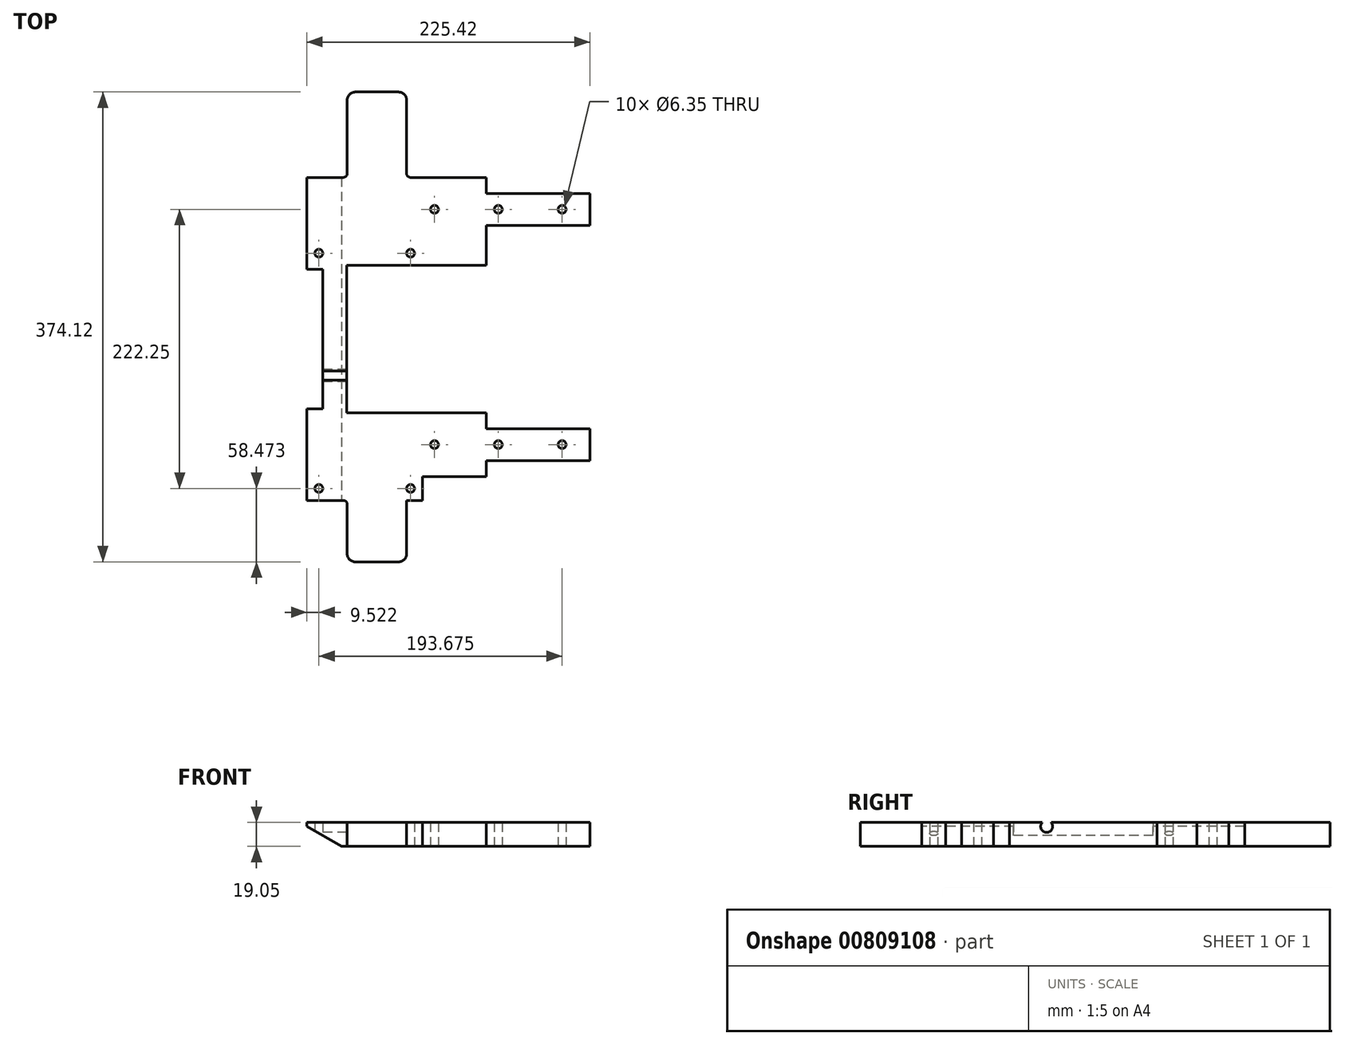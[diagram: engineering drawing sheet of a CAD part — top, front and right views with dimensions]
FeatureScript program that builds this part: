
annotation { "Feature Type Name" : "Feature", "Feature Type Description" : "" }
export const myFeature = defineFeature(function(context is Context, id is Id, definition is map)
    precondition{}
    {
        {
            var Q0;
            Q0=qCreatedBy(makeId("Top.planeOp"),FACE);
            var sketch = newSketch(context, id + "F0", { "sketchPlane" : qUnion([Q0])});
            skLineSegment(sketch, "E0.top", {"start": v(-147.88, 53.82) * mm, "end": v(-118.93, 53.82) * mm});
            skLineSegment(sketch, "E0.right", {"start": v(1.34, 15.72) * mm, "end": v(1.34, 41.12) * mm, "construction": true});
            skLineSegment(sketch, "E1.top", {"start": v(77.54, 41.12) * mm, "end": v(-5, 41.12) * mm});
            skLineSegment(sketch, "E1.right", {"start": v(-5, 53.82) * mm, "end": v(-5, 41.12) * mm});
            skLineSegment(sketch, "E2.top", {"start": v(77.54, 15.72) * mm, "end": v(77.54, 15.72) * mm});
            skLineSegment(sketch, "E2.right", {"start": v(-5, -16.03) * mm, "end": v(-5, 15.72) * mm});
            skLineSegment(sketch, "E3.0", {"start": v(-68.5, 115.47) * mm, "end": v(-68.5, 57) * mm});
            skLineSegment(sketch, "E4.0", {"start": v(-109.4, 121.82) * mm, "end": v(-74.86, 121.82) * mm});
            skLineSegment(sketch, "E5.0", {"start": v(-115.75, 115.47) * mm, "end": v(-115.75, 57) * mm});
            skLineSegment(sketch, "E6.trimOffspring", {"start": v(-65.33, 53.82) * mm, "end": v(-5, 53.82) * mm});
            skPoint(sketch, "E7.visualSharp", {"position": v(-115.75, 121.82) * mm});
            skArc(sketch, "E7.filletArc", {"start": v(-109.4, 121.82) * mm, "mid": v(-113.9, 119.96) * mm, "end": v(-115.75, 115.47) * mm});
            skPoint(sketch, "E8.visualSharp", {"position": v(-68.5, 121.82) * mm});
            skArc(sketch, "E8.filletArc", {"start": v(-68.5, 115.47) * mm, "mid": v(-70.37, 119.96) * mm, "end": v(-74.86, 121.82) * mm});
            skLineSegment(sketch, "E9.0", {"start": v(-109.78, -65.24) * mm, "end": v(-5, -65.24) * mm, "construction": true});
            skArc(sketch, "E10.MirrorCS", {"start": v(-109.4, -252.3) * mm, "mid": v(-113.9, -250.44) * mm, "end": v(-115.75, -245.95) * mm});
            skArc(sketch, "E11.MirrorCS", {"start": v(-68.5, -245.95) * mm, "mid": v(-70.37, -250.44) * mm, "end": v(-74.86, -252.3) * mm});
            skLineSegment(sketch, "E12.MirrorCS", {"start": v(-5, -184.3) * mm, "end": v(-5, -171.6) * mm});
            skLineSegment(sketch, "E13.MirrorCS", {"start": v(77.54, -171.6) * mm, "end": v(-5, -171.6) * mm});
            skLineSegment(sketch, "E14.MirrorCS", {"start": v(77.54, -146.2) * mm, "end": v(-5, -146.2) * mm});
            skLineSegment(sketch, "E15.MirrorCS", {"start": v(-5, -122.48) * mm, "end": v(-5, -146.2) * mm});
            skLineSegment(sketch, "E16.MirrorCS", {"start": v(-147.88, -184.3) * mm, "end": v(-138.36, -184.3) * mm, "construction": true});
            skLineSegment(sketch, "E17.MirrorCS", {"start": v(1.34, -146.2) * mm, "end": v(1.34, -171.6) * mm, "construction": true});
            skLineSegment(sketch, "E18.MirrorCS", {"start": v(-147.88, -171.6) * mm, "end": v(-138.36, -171.6) * mm, "construction": true});
            skLineSegment(sketch, "E19.MirrorCS", {"start": v(-109.4, -252.3) * mm, "end": v(-74.86, -252.3) * mm});
            skLineSegment(sketch, "E20.MirrorCS", {"start": v(-68.5, -245.95) * mm, "end": v(-68.5, -203.35) * mm});
            skLineSegment(sketch, "E21.MirrorCS", {"start": v(-115.75, -245.95) * mm, "end": v(-115.75, -206.53) * mm});
            skPoint(sketch, "E22.MirrorP", {"position": v(-68.5, -252.3) * mm});
            skLineSegment(sketch, "E23.MirrorCS", {"start": v(-116.13, -133.5) * mm, "end": v(-5, -133.5) * mm});
            skPoint(sketch, "E24.MirrorP", {"position": v(-115.75, -252.3) * mm});
            skLineSegment(sketch, "E25.MirrorCS", {"start": v(-147.88, -203.35) * mm, "end": v(-118.93, -203.35) * mm});
            skLineSegment(sketch, "E26.0", {"start": v(-109.78, -9.68) * mm, "end": v(-5, -9.68) * mm, "construction": true});
            skLineSegment(sketch, "E27.0", {"start": v(-109.78, -120.8) * mm, "end": v(-5, -120.8) * mm, "construction": true});
            skArc(sketch, "E28", {"start": v(-3.65, -119.88) * mm, "mid": v(24.81, -65.24) * mm, "end": v(-3.65, -10.6) * mm});
            skArc(sketch, "E29.0", {"start": v(-15.54, -104.93) * mm, "mid": v(5.76, -65.24) * mm, "end": v(-15.54, -25.55) * mm});
            skLineSegment(sketch, "E30.0", {"start": v(-24.06, -9.68) * mm, "end": v(-24.06, -0.15) * mm});
            skLineSegment(sketch, "E31.0", {"start": v(-24.06, -120.8) * mm, "end": v(-24.06, -130.33) * mm});
            skPoint(sketch, "E32.orphan", {"position": v(-5, 3.02) * mm});
            skPoint(sketch, "E33.visualSharp", {"position": v(-24.06, -21.07) * mm});
            skArc(sketch, "E33.filletArc", {"start": v(-24.06, -9.68) * mm, "mid": v(-21.8, -18.69) * mm, "end": v(-15.54, -25.55) * mm});
            skPoint(sketch, "E34.visualSharp", {"position": v(-24.06, -109.41) * mm});
            skArc(sketch, "E34.filletArc", {"start": v(-15.54, -104.93) * mm, "mid": v(-21.8, -111.8) * mm, "end": v(-24.06, -120.8) * mm});
            skLineSegment(sketch, "E35.0", {"start": v(-116.13, -16.03) * mm, "end": v(-5, -16.03) * mm});
            skPoint(sketch, "E36.right.end.orphan", {"position": v(-97.08, 41.12) * mm});
            skLineSegment(sketch, "E37.trimOffspring", {"start": v(-112.58, 3.02) * mm, "end": v(-27.23, 3.02) * mm});
            skArc(sketch, "E38.filletArc", {"start": v(-115.75, -206.53) * mm, "mid": v(-116.68, -204.28) * mm, "end": v(-118.93, -203.35) * mm});
            skPoint(sketch, "E39.visualSharp", {"position": v(-24.06, -133.5) * mm});
            skArc(sketch, "E39.filletArc", {"start": v(-27.23, -133.5) * mm, "mid": v(-24.99, -132.57) * mm, "end": v(-24.06, -130.33) * mm});
            skPoint(sketch, "E40.visualSharp", {"position": v(-24.06, 3.02) * mm});
            skArc(sketch, "E40.filletArc", {"start": v(-24.06, -0.15) * mm, "mid": v(-24.99, 2.1) * mm, "end": v(-27.23, 3.02) * mm});
            skPoint(sketch, "E41.visualSharp", {"position": v(-115.75, 53.82) * mm});
            skArc(sketch, "E41.filletArc", {"start": v(-118.93, 53.82) * mm, "mid": v(-116.68, 54.75) * mm, "end": v(-115.75, 57) * mm});
            skPoint(sketch, "E42.visualSharp", {"position": v(-68.5, 53.82) * mm});
            skArc(sketch, "E42.filletArc", {"start": v(-68.5, 57) * mm, "mid": v(-67.58, 54.75) * mm, "end": v(-65.33, 53.82) * mm});
            skArc(sketch, "E43.filletArc", {"start": v(-3.65, -119.88) * mm, "mid": v(-4.65, -121.01) * mm, "end": v(-5, -122.48) * mm});
            skArc(sketch, "E44.filletArc", {"start": v(-5, -8) * mm, "mid": v(-4.65, -9.47) * mm, "end": v(-3.65, -10.6) * mm});
            skLineSegment(sketch, "E45.trimOffspring", {"start": v(-68.5, -203.35) * mm, "end": v(-55.8, -203.35) * mm});
            skLineSegment(sketch, "E46.0", {"start": v(-49.46, -146.2) * mm, "end": v(-49.46, -184.3) * mm, "construction": true});
            skLineSegment(sketch, "E47.0", {"start": v(52.14, -146.2) * mm, "end": v(52.14, -171.6) * mm, "construction": true});
            skLineSegment(sketch, "E48.0", {"start": v(-147.88, 53.82) * mm, "end": v(-147.88, -16.03) * mm});
            skLineSegment(sketch, "E49.0", {"start": v(-147.88, -171.6) * mm, "end": v(-147.88, -203.35) * mm});
            skLineSegment(sketch, "E50.0", {"start": v(-135.18, -181.13) * mm, "end": v(-135.18, -174.78) * mm, "construction": true});
            skPoint(sketch, "E51.visualSharp", {"position": v(-135.18, -184.3) * mm});
            skArc(sketch, "E51.filletArc", {"start": v(-138.36, -184.3) * mm, "mid": v(-136.11, -183.37) * mm, "end": v(-135.18, -181.13) * mm, "construction": true});
            skPoint(sketch, "E52.visualSharp", {"position": v(-135.18, -171.6) * mm});
            skArc(sketch, "E52.filletArc", {"start": v(-135.18, -174.78) * mm, "mid": v(-136.11, -172.53) * mm, "end": v(-138.36, -171.6) * mm, "construction": true});
            skPoint(sketch, "E53.visualSharp", {"position": v(-147.88, -133.5) * mm});
            skArc(sketch, "E53.filletArc", {"start": v(-144.7, -133.5) * mm, "mid": v(-146.95, -134.43) * mm, "end": v(-147.88, -136.68) * mm});
            skPoint(sketch, "E54.visualSharp", {"position": v(-147.88, -203.35) * mm});
            skLineSegment(sketch, "E55.0", {"start": v(-5, -184.3) * mm, "end": v(-55.8, -184.3) * mm});
            skLineSegment(sketch, "E56", {"start": v(-49.46, -184.3) * mm, "end": v(-49.46, -203.35) * mm, "construction": true});
            skLineSegment(sketch, "E57.0", {"start": v(-55.8, -184.3) * mm, "end": v(-55.8, -203.35) * mm});
            skLineSegment(sketch, "E58", {"start": v(-55.8, -203.35) * mm, "end": v(-49.46, -203.35) * mm, "construction": true});
            skLineSegment(sketch, "E59.0", {"start": v(77.54, 41.12) * mm, "end": v(77.54, 15.72) * mm});
            skLineSegment(sketch, "E60", {"start": v(77.54, 15.72) * mm, "end": v(-5, 15.72) * mm});
            skLineSegment(sketch, "E61", {"start": v(77.54, -146.2) * mm, "end": v(77.54, -171.6) * mm});
            skLineSegment(sketch, "E62", {"start": v(77.54, 15.72) * mm, "end": v(77.54, -146.2) * mm, "construction": true});
            skLineSegment(sketch, "E63.trimOffspring", {"start": v(-147.88, -16.03) * mm, "end": v(-147.88, -171.6) * mm});
            skLineSegment(sketch, "E64.0", {"start": v(-116.13, -16.03) * mm, "end": v(-116.13, -133.5) * mm});
            skLineSegment(sketch, "E65.bottom", {"start": v(-147.88, -130.33) * mm, "end": v(-135.18, -130.33) * mm});
            skLineSegment(sketch, "E65.top", {"start": v(-147.88, -19.2) * mm, "end": v(-135.18, -19.2) * mm});
            skLineSegment(sketch, "E65.left", {"start": v(-147.88, -130.33) * mm, "end": v(-147.88, -19.2) * mm});
            skLineSegment(sketch, "E65.right", {"start": v(-135.18, -130.33) * mm, "end": v(-135.18, -19.2) * mm});
            skCircle(sketch, "E66", {"center": v(-138.36, -193.83) * mm, "radius": 3.18 * mm});
            skCircle(sketch, "E67.0.1.0", {"center": v(-138.36, -6.5) * mm, "radius": 3.18 * mm});
            skCircle(sketch, "E67.1.0.0", {"center": v(-65.33, -193.83) * mm, "radius": 3.18 * mm});
            skCircle(sketch, "E67.1.1.0", {"center": v(-65.33, -6.5) * mm, "radius": 3.18 * mm});
            skLineSegment(sketch, "E67.direction1", {"start": v(-138.36, -193.83) * mm, "end": v(-65.33, -193.83) * mm, "construction": true});
            skLineSegment(sketch, "E67.direction2", {"start": v(-138.36, -193.83) * mm, "end": v(-138.36, -6.5) * mm, "construction": true});
            skCircle(sketch, "E68", {"center": v(-46.28, -158.9) * mm, "radius": 3.18 * mm});
            skCircle(sketch, "E69.0.1.0", {"center": v(-46.28, 28.42) * mm, "radius": 3.18 * mm});
            skCircle(sketch, "E69.1.0.0", {"center": v(4.52, -158.9) * mm, "radius": 3.18 * mm});
            skCircle(sketch, "E69.1.1.0", {"center": v(4.52, 28.42) * mm, "radius": 3.18 * mm});
            skCircle(sketch, "E69.2.0.0", {"center": v(55.32, -158.9) * mm, "radius": 3.18 * mm});
            skCircle(sketch, "E69.2.1.0", {"center": v(55.32, 28.42) * mm, "radius": 3.18 * mm});
            skLineSegment(sketch, "E69.direction1", {"start": v(-46.28, -158.9) * mm, "end": v(4.52, -158.9) * mm, "construction": true});
            skLineSegment(sketch, "E69.direction2", {"start": v(-46.28, -158.9) * mm, "end": v(-46.28, 28.42) * mm, "construction": true});
            skSolve(sketch);
        }
        {
            var Q0;
            Q0=makeQuery(id+"F0.imprint","IMPRINT",FACE,{"disambiguationData":[TD([[makeQuery(id+"F0.imprint","IMPRINT",EDGE,{"derivedFrom":sQuery(id+"F0.wireOp",EDGE,"E0.top")}),-1.0]])]});
            extrude(context, id + "F1", {"entities" : qUnion([Q0]), "depth" : 19.05 * mm, "offsetDistance" : 25.4 * mm});
        }
        {
            var Q0;
            Q0=makeQuery(id+"F1.opExtrude","SWEPT_FACE",FACE,{"disambiguationData":[OSD([sQuery(id+"F0.wireOp",EDGE,"E48.0"),sQuery(id+"F0.wireOp",EDGE,"E49.0"),sQuery(id+"F0.wireOp",EDGE,"E63.trimOffspring")])]});
            var sketch = newSketch(context, id + "F2", { "sketchPlane" : qUnion([Q0])});
            skCircle(sketch, "E70", {"center": v(103.94, 15.88) * mm, "radius": 4.79 * mm});
            skPoint(sketch, "E70.centerSnap0", {"position": v(-53.82, 15.87) * mm});
            skLineSegment(sketch, "E71.direction1", {"start": v(103.94, 15.88) * mm, "end": v(40.44, 15.87) * mm, "construction": true});
            skSolve(sketch);
        }
        {
            var Q0;
            Q0=makeQuery(id+"F2.imprint","IMPRINT",FACE,{"disambiguationData":[TD([[makeQuery(id+"F2.imprint","IMPRINT",EDGE,{"derivedFrom":sQuery(id+"F2.wireOp",EDGE,"E70")}),1.0]])]});
            var Q1;
            Q1=makeQuery(id+"F2.imprint","IMPRINT",FACE,{"disambiguationData":[TD([[makeQuery(id+"F2.imprint","IMPRINT",EDGE,{"derivedFrom":sQuery(id+"F2.wireOp",EDGE,"E71.1.0.0")}),1.0]])]});
            extrude(context, id + "F3", {"entities" : qUnion([Q0, Q1]), "operationType" : NewBodyOperationType.REMOVE, "oppositeDirection" : true, "depth" : 50.8 * mm, "offsetDistance" : 25.4 * mm});
        }
        {
            var Q0;
            Q0=makeQuery(id+"F1.opExtrude","SWEPT_FACE",FACE,{"disambiguationData":[OSD([sQuery(id+"F0.wireOp",EDGE,"E25.MirrorCS")])]});
            var sketch = newSketch(context, id + "F4", { "sketchPlane" : qUnion([Q0])});
            skLineSegment(sketch, "E72", {"start": v(-147.88, 15.88) * mm, "end": v(-120.39, 0) * mm});
            skSolve(sketch);
        }
        {
            var Q0;
            Q0 = qSketchRegion(id + "F4", true);
            var Q1;
            {var subQ0=sQuery(id+"F4.wireOp",EDGE,"E72");Q1=makeQuery(id+"F4.imprint","IMPRINT",FACE,{"disambiguationData":[TD([[makeQuery(id+"F4.imprint","IMPRINT",EDGE,{"derivedFrom":subQ0}),-1.0]])]});}
            extrude(context, id + "F5", {"entities" : qUnion([Q0, Q1]), "operationType" : NewBodyOperationType.REMOVE, "oppositeDirection" : true, "depth" : 279.4 * mm, "offsetDistance" : 25.4 * mm});
        }
    });
